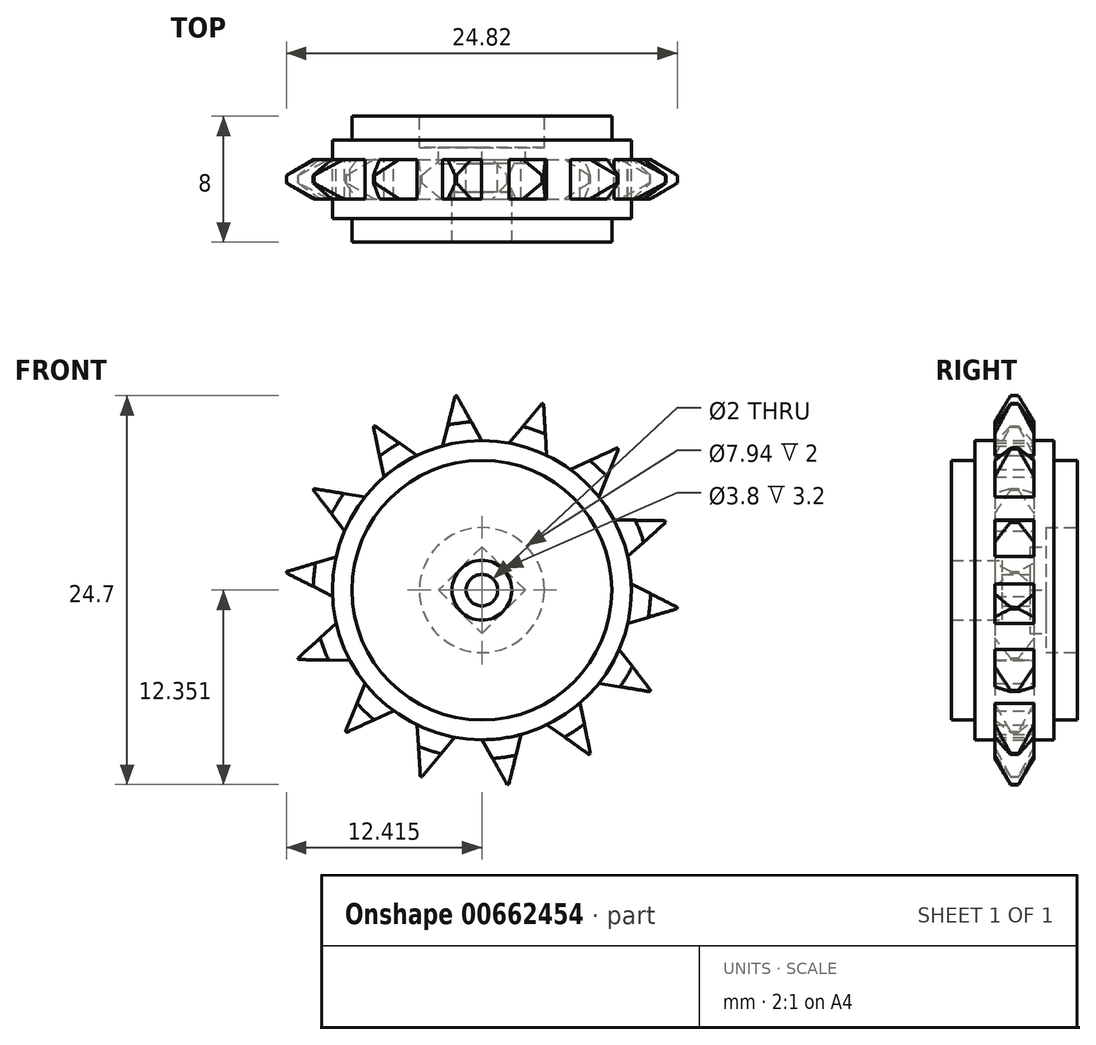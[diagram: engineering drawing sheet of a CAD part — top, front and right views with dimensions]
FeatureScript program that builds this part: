
annotation { "Feature Type Name" : "Feature", "Feature Type Description" : "" }
export const myFeature = defineFeature(function(context is Context, id is Id, definition is map)
    precondition{}
    {
        {
            var Q0;
            Q0=qCreatedBy(makeId("Front.planeOp"),FACE);
            var sketch = newSketch(context, id + "F0", { "sketchPlane" : qUnion([Q0])});
            skCircle(sketch, "E0.cCircle", {"center": v(-41.57, 57.03) * mm, "radius": 16.12 * mm, "construction": true});
            skLineSegment(sketch, "E0.0", {"start": v(-32.25, 43.87) * mm, "end": v(-37.32, 41.48) * mm});
            skLineSegment(sketch, "E0.1", {"start": v(-37.32, 41.48) * mm, "end": v(-42.9, 40.96) * mm});
            skLineSegment(sketch, "E0.2", {"start": v(-42.9, 40.96) * mm, "end": v(-48.3, 42.38) * mm});
            skLineSegment(sketch, "E0.3", {"start": v(-48.3, 42.38) * mm, "end": v(-52.91, 45.57) * mm});
            skLineSegment(sketch, "E0.4", {"start": v(-52.91, 45.57) * mm, "end": v(-56.15, 50.14) * mm});
            skLineSegment(sketch, "E0.5", {"start": v(-56.15, 50.14) * mm, "end": v(-57.63, 55.54) * mm});
            skLineSegment(sketch, "E0.6", {"start": v(-57.63, 55.54) * mm, "end": v(-57.17, 61.12) * mm});
            skLineSegment(sketch, "E0.7", {"start": v(-57.17, 61.12) * mm, "end": v(-54.83, 66.2) * mm});
            skLineSegment(sketch, "E0.8", {"start": v(-54.83, 66.2) * mm, "end": v(-50.9, 70.19) * mm});
            skLineSegment(sketch, "E0.9", {"start": v(-50.9, 70.19) * mm, "end": v(-45.83, 72.58) * mm});
            skLineSegment(sketch, "E0.10", {"start": v(-45.83, 72.58) * mm, "end": v(-40.25, 73.1) * mm});
            skLineSegment(sketch, "E0.11", {"start": v(-40.25, 73.1) * mm, "end": v(-34.84, 71.68) * mm});
            skLineSegment(sketch, "E0.12", {"start": v(-34.84, 71.68) * mm, "end": v(-30.23, 68.5) * mm});
            skLineSegment(sketch, "E0.13", {"start": v(-30.23, 68.5) * mm, "end": v(-27, 63.92) * mm});
            skLineSegment(sketch, "E0.14", {"start": v(-27, 63.92) * mm, "end": v(-25.52, 58.52) * mm});
            skLineSegment(sketch, "E0.15", {"start": v(-25.52, 58.52) * mm, "end": v(-25.98, 52.94) * mm});
            skLineSegment(sketch, "E0.16", {"start": v(-25.98, 52.94) * mm, "end": v(-28.31, 47.85) * mm});
            skLineSegment(sketch, "E0.17", {"start": v(-28.31, 47.85) * mm, "end": v(-32.25, 43.87) * mm});
            skCircle(sketch, "E1.cCircle", {"center": v(18.75, 75.94) * mm, "radius": 12.58 * mm, "construction": true});
            skLineSegment(sketch, "E1.0", {"start": v(29.55, 69.47) * mm, "end": v(25.67, 65.43) * mm});
            skLineSegment(sketch, "E1.1", {"start": v(25.67, 65.43) * mm, "end": v(20.43, 63.47) * mm});
            skLineSegment(sketch, "E1.2", {"start": v(20.43, 63.47) * mm, "end": v(14.85, 63.98) * mm});
            skLineSegment(sketch, "E1.3", {"start": v(14.85, 63.98) * mm, "end": v(10.05, 66.86) * mm});
            skLineSegment(sketch, "E1.4", {"start": v(10.05, 66.86) * mm, "end": v(6.97, 71.54) * mm});
            skLineSegment(sketch, "E1.5", {"start": v(6.97, 71.54) * mm, "end": v(6.22, 77.09) * mm});
            skLineSegment(sketch, "E1.6", {"start": v(6.22, 77.09) * mm, "end": v(7.96, 82.4) * mm});
            skLineSegment(sketch, "E1.7", {"start": v(7.96, 82.4) * mm, "end": v(11.84, 86.45) * mm});
            skLineSegment(sketch, "E1.8", {"start": v(11.84, 86.45) * mm, "end": v(17.08, 88.41) * mm});
            skLineSegment(sketch, "E1.9", {"start": v(17.08, 88.41) * mm, "end": v(22.66, 87.9) * mm});
            skLineSegment(sketch, "E1.10", {"start": v(22.66, 87.9) * mm, "end": v(27.46, 85.02) * mm});
            skLineSegment(sketch, "E1.11", {"start": v(27.46, 85.02) * mm, "end": v(30.54, 80.35) * mm});
            skLineSegment(sketch, "E1.12", {"start": v(30.54, 80.35) * mm, "end": v(31.29, 74.8) * mm});
            skLineSegment(sketch, "E1.13", {"start": v(31.29, 74.8) * mm, "end": v(29.55, 69.47) * mm});
            skLineSegment(sketch, "E2", {"start": v(7.96, 82.4) * mm, "end": v(18.75, 75.94) * mm});
            skLineSegment(sketch, "E3", {"start": v(18.75, 75.94) * mm, "end": v(17.08, 88.41) * mm});
            skLineSegment(sketch, "E4", {"start": v(13.36, 79.18) * mm, "end": v(11.84, 86.45) * mm});
            skLineSegment(sketch, "E5", {"start": v(17.92, 82.18) * mm, "end": v(11.84, 86.45) * mm});
            skLineSegment(sketch, "E6.1.0", {"start": v(15.3, 81.2) * mm, "end": v(7.96, 82.4) * mm});
            skLineSegment(sketch, "E6.1.1", {"start": v(12.49, 76.51) * mm, "end": v(7.96, 82.4) * mm});
            skLineSegment(sketch, "E6.2.0", {"start": v(13.36, 79.18) * mm, "end": v(6.22, 77.09) * mm});
            skLineSegment(sketch, "E6.2.1", {"start": v(12.86, 73.74) * mm, "end": v(6.22, 77.09) * mm});
            skLineSegment(sketch, "E6.3.0", {"start": v(12.49, 76.51) * mm, "end": v(6.97, 71.54) * mm});
            skLineSegment(sketch, "E6.3.1", {"start": v(14.4, 71.4) * mm, "end": v(6.97, 71.54) * mm});
            skLineSegment(sketch, "E6.4.0", {"start": v(12.86, 73.74) * mm, "end": v(10.05, 66.86) * mm});
            skLineSegment(sketch, "E6.4.1", {"start": v(16.8, 69.96) * mm, "end": v(10.05, 66.86) * mm});
            skLineSegment(sketch, "E6.5.0", {"start": v(14.4, 71.4) * mm, "end": v(14.85, 63.98) * mm});
            skLineSegment(sketch, "E6.5.1", {"start": v(19.6, 69.7) * mm, "end": v(14.85, 63.98) * mm});
            skLineSegment(sketch, "E6.6.0", {"start": v(16.8, 69.96) * mm, "end": v(20.43, 63.47) * mm});
            skLineSegment(sketch, "E6.6.1", {"start": v(22.21, 70.69) * mm, "end": v(20.43, 63.47) * mm});
            skLineSegment(sketch, "E6.7.0", {"start": v(19.6, 69.7) * mm, "end": v(25.67, 65.43) * mm});
            skLineSegment(sketch, "E6.7.1", {"start": v(24.15, 72.7) * mm, "end": v(25.67, 65.43) * mm});
            skLineSegment(sketch, "E6.8.0", {"start": v(22.21, 70.69) * mm, "end": v(29.55, 69.47) * mm});
            skLineSegment(sketch, "E6.8.1", {"start": v(25.02, 75.37) * mm, "end": v(29.55, 69.47) * mm});
            skLineSegment(sketch, "E6.9.0", {"start": v(24.15, 72.7) * mm, "end": v(31.29, 74.8) * mm});
            skLineSegment(sketch, "E6.9.1", {"start": v(24.65, 78.14) * mm, "end": v(31.29, 74.8) * mm});
            skLineSegment(sketch, "E6.10.0", {"start": v(25.02, 75.37) * mm, "end": v(30.54, 80.35) * mm});
            skLineSegment(sketch, "E6.10.1", {"start": v(23.1, 80.48) * mm, "end": v(30.54, 80.35) * mm});
            skLineSegment(sketch, "E6.11.0", {"start": v(24.65, 78.14) * mm, "end": v(27.46, 85.02) * mm});
            skLineSegment(sketch, "E6.11.1", {"start": v(20.7, 81.92) * mm, "end": v(27.46, 85.02) * mm});
            skLineSegment(sketch, "E6.12.0", {"start": v(23.1, 80.48) * mm, "end": v(22.66, 87.9) * mm});
            skLineSegment(sketch, "E6.12.1", {"start": v(17.92, 82.18) * mm, "end": v(22.66, 87.9) * mm});
            skLineSegment(sketch, "E6.13.0", {"start": v(20.7, 81.92) * mm, "end": v(17.08, 88.41) * mm});
            skLineSegment(sketch, "E6.13.1", {"start": v(15.3, 81.2) * mm, "end": v(17.08, 88.41) * mm});
            skCircle(sketch, "E7", {"center": v(18.75, 75.94) * mm, "radius": 12.46 * mm});
            skCircle(sketch, "E8", {"center": v(18.75, 75.94) * mm, "radius": 9.5 * mm});
            skCircle(sketch, "E9", {"center": v(18.75, 75.94) * mm, "radius": 8.25 * mm});
            skCircle(sketch, "E10.cCircle", {"center": v(18.75, 75.94) * mm, "radius": 2.65 * mm, "construction": true});
            skLineSegment(sketch, "E10.0", {"start": v(16.1, 75.94) * mm, "end": v(18.75, 78.6) * mm});
            skLineSegment(sketch, "E10.1", {"start": v(18.75, 78.6) * mm, "end": v(21.4, 75.94) * mm});
            skLineSegment(sketch, "E10.2", {"start": v(21.4, 75.94) * mm, "end": v(18.75, 73.29) * mm});
            skLineSegment(sketch, "E10.3", {"start": v(18.75, 73.29) * mm, "end": v(16.1, 75.94) * mm});
            skCircle(sketch, "E11", {"center": v(18.75, 75.94) * mm, "radius": 0.86 * mm});
            skSolve(sketch);
        }
        {
            var Q0;
            {var subQ27=sQuery(id+"F0.wireOp",EDGE,"E6.3.0");var subQ28=sQuery(id+"F0.wireOp",EDGE,"E6.1.1");var subQ29=makeQuery(id+"F0.imprint","INTERSECT",VERTEX,{"derivedFrom":[subQ28,subQ27]});Q0=makeQuery(id+"F0.imprint","IMPRINT",FACE,{"disambiguationData":[TD([[makeQuery(id+"F0.imprint","IMPRINT",EDGE,{"disambiguationData":[TD([[subQ29,-1.0]])],"derivedFrom":subQ28}),-1.0]])]});}
            var Q1;
            {var subQ3=sQuery(id+"F0.wireOp",EDGE,"E6.13.1");var subQ9=sQuery(id+"F0.wireOp",EDGE,"E6.1.0");var subQ11=makeQuery(id+"F0.imprint","INTERSECT",VERTEX,{"derivedFrom":[subQ9,subQ3]});Q1=makeQuery(id+"F0.imprint","IMPRINT",FACE,{"disambiguationData":[TD([[makeQuery(id+"F0.imprint","IMPRINT",EDGE,{"disambiguationData":[TD([[subQ11,-1.0]])],"derivedFrom":subQ9}),1.0]])]});}
            var Q2;
            {var subQ1=sQuery(id+"F0.wireOp",EDGE,"E6.1.0");var subQ5=sQuery(id+"F0.wireOp",EDGE,"E4");var subQ6=makeQuery(id+"F0.imprint","INTERSECT",VERTEX,{"derivedFrom":[subQ5,subQ1]});Q2=makeQuery(id+"F0.imprint","IMPRINT",FACE,{"disambiguationData":[TD([[makeQuery(id+"F0.imprint","IMPRINT",EDGE,{"disambiguationData":[TD([[subQ6,-1.0]])],"derivedFrom":subQ5}),-1.0]])]});}
            var Q3;
            {var subQ0=sQuery(id+"F0.wireOp",EDGE,"E6.2.0");var subQ5=sQuery(id+"F0.wireOp",EDGE,"E6.1.1");var subQ6=makeQuery(id+"F0.imprint","INTERSECT",VERTEX,{"derivedFrom":[subQ5,subQ0]});Q3=makeQuery(id+"F0.imprint","IMPRINT",FACE,{"disambiguationData":[TD([[makeQuery(id+"F0.imprint","IMPRINT",EDGE,{"disambiguationData":[TD([[subQ6,-1.0]])],"derivedFrom":subQ5}),-1.0]])]});}
            var Q4;
            {var subQ0=sQuery(id+"F0.wireOp",EDGE,"E6.3.0");var subQ1=sQuery(id+"F0.wireOp",EDGE,"E6.1.1");var subQ2=makeQuery(id+"F0.imprint","INTERSECT",VERTEX,{"derivedFrom":[subQ1,subQ0]});Q4=makeQuery(id+"F0.imprint","IMPRINT",FACE,{"disambiguationData":[TD([[makeQuery(id+"F0.imprint","IMPRINT",EDGE,{"disambiguationData":[TD([[subQ2,-1.0]])],"derivedFrom":subQ1}),1.0]])]});}
            var Q5;
            {var subQ0=sQuery(id+"F0.wireOp",EDGE,"E6.3.0");var subQ1=sQuery(id+"F0.wireOp",EDGE,"E6.2.1");var subQ2=makeQuery(id+"F0.imprint","INTERSECT",VERTEX,{"derivedFrom":[subQ1,subQ0]});Q5=makeQuery(id+"F0.imprint","IMPRINT",FACE,{"disambiguationData":[TD([[makeQuery(id+"F0.imprint","IMPRINT",EDGE,{"disambiguationData":[TD([[subQ2,-1.0]])],"derivedFrom":subQ1}),1.0]])]});}
            var Q6;
            {var subQ0=sQuery(id+"F0.wireOp",EDGE,"E6.2.0");var subQ1=sQuery(id+"F0.wireOp",EDGE,"E6.1.1");var subQ2=makeQuery(id+"F0.imprint","INTERSECT",VERTEX,{"derivedFrom":[subQ1,subQ0]});Q6=makeQuery(id+"F0.imprint","IMPRINT",FACE,{"disambiguationData":[TD([[makeQuery(id+"F0.imprint","IMPRINT",EDGE,{"disambiguationData":[TD([[subQ2,-1.0]])],"derivedFrom":subQ1}),1.0]])]});}
            var Q7;
            {var subQ0=sQuery(id+"F0.wireOp",EDGE,"E4");var subQ5=sQuery(id+"F0.wireOp",EDGE,"E6.1.0");var subQ6=makeQuery(id+"F0.imprint","INTERSECT",VERTEX,{"derivedFrom":[subQ0,subQ5]});Q7=makeQuery(id+"F0.imprint","IMPRINT",FACE,{"disambiguationData":[TD([[makeQuery(id+"F0.imprint","IMPRINT",EDGE,{"disambiguationData":[TD([[subQ6,-1.0]])],"derivedFrom":subQ5}),1.0]])]});}
            var Q8;
            {var subQ0=sQuery(id+"F0.wireOp",EDGE,"E6.1.0");var subQ1=sQuery(id+"F0.wireOp",EDGE,"E4");var subQ2=makeQuery(id+"F0.imprint","INTERSECT",VERTEX,{"derivedFrom":[subQ1,subQ0]});Q8=makeQuery(id+"F0.imprint","IMPRINT",FACE,{"disambiguationData":[TD([[makeQuery(id+"F0.imprint","IMPRINT",EDGE,{"disambiguationData":[TD([[subQ2,-1.0]])],"derivedFrom":subQ1}),1.0]])]});}
            var Q9;
            {var subQ0=sQuery(id+"F0.wireOp",EDGE,"E6.13.1");var subQ1=sQuery(id+"F0.wireOp",EDGE,"E5");var subQ2=makeQuery(id+"F0.imprint","INTERSECT",VERTEX,{"derivedFrom":[subQ1,subQ0]});Q9=makeQuery(id+"F0.imprint","IMPRINT",FACE,{"disambiguationData":[TD([[makeQuery(id+"F0.imprint","IMPRINT",EDGE,{"disambiguationData":[TD([[subQ2,-1.0]])],"derivedFrom":subQ1}),-1.0]])]});}
            var Q10;
            {var subQ0=sQuery(id+"F0.wireOp",EDGE,"E5");var subQ5=sQuery(id+"F0.wireOp",EDGE,"E6.13.1");var subQ7=makeQuery(id+"F0.imprint","INTERSECT",VERTEX,{"derivedFrom":[subQ0,subQ5]});Q10=makeQuery(id+"F0.imprint","IMPRINT",FACE,{"disambiguationData":[TD([[makeQuery(id+"F0.imprint","IMPRINT",EDGE,{"disambiguationData":[TD([[subQ7,-1.0]])],"derivedFrom":subQ5}),-1.0]])]});}
            var Q11;
            {var subQ0=sQuery(id+"F0.wireOp",EDGE,"E6.12.1");var subQ5=sQuery(id+"F0.wireOp",EDGE,"E6.13.0");var subQ6=makeQuery(id+"F0.imprint","INTERSECT",VERTEX,{"derivedFrom":[subQ0,subQ5]});Q11=makeQuery(id+"F0.imprint","IMPRINT",FACE,{"disambiguationData":[TD([[makeQuery(id+"F0.imprint","IMPRINT",EDGE,{"disambiguationData":[TD([[subQ6,-1.0]])],"derivedFrom":subQ5}),1.0]])]});}
            var Q12;
            {var subQ0=sQuery(id+"F0.wireOp",EDGE,"E6.13.0");var subQ1=sQuery(id+"F0.wireOp",EDGE,"E6.12.1");var subQ2=makeQuery(id+"F0.imprint","INTERSECT",VERTEX,{"derivedFrom":[subQ1,subQ0]});Q12=makeQuery(id+"F0.imprint","IMPRINT",FACE,{"disambiguationData":[TD([[makeQuery(id+"F0.imprint","IMPRINT",EDGE,{"disambiguationData":[TD([[subQ2,-1.0]])],"derivedFrom":subQ1}),1.0]])]});}
            var Q13;
            {var subQ0=sQuery(id+"F0.wireOp",EDGE,"E6.13.0");var subQ1=sQuery(id+"F0.wireOp",EDGE,"E6.11.1");var subQ2=makeQuery(id+"F0.imprint","INTERSECT",VERTEX,{"derivedFrom":[subQ1,subQ0]});Q13=makeQuery(id+"F0.imprint","IMPRINT",FACE,{"disambiguationData":[TD([[makeQuery(id+"F0.imprint","IMPRINT",EDGE,{"disambiguationData":[TD([[subQ2,-1.0]])],"derivedFrom":subQ1}),1.0]])]});}
            var Q14;
            {var subQ0=sQuery(id+"F0.wireOp",EDGE,"E6.12.0");var subQ1=sQuery(id+"F0.wireOp",EDGE,"E6.11.1");var subQ2=makeQuery(id+"F0.imprint","INTERSECT",VERTEX,{"derivedFrom":[subQ1,subQ0]});Q14=makeQuery(id+"F0.imprint","IMPRINT",FACE,{"disambiguationData":[TD([[makeQuery(id+"F0.imprint","IMPRINT",EDGE,{"disambiguationData":[TD([[subQ2,-1.0]])],"derivedFrom":subQ1}),1.0]])]});}
            var Q15;
            {var subQ0=sQuery(id+"F0.wireOp",EDGE,"E6.12.0");var subQ1=sQuery(id+"F0.wireOp",EDGE,"E6.10.1");var subQ2=makeQuery(id+"F0.imprint","INTERSECT",VERTEX,{"derivedFrom":[subQ1,subQ0]});Q15=makeQuery(id+"F0.imprint","IMPRINT",FACE,{"disambiguationData":[TD([[makeQuery(id+"F0.imprint","IMPRINT",EDGE,{"disambiguationData":[TD([[subQ2,-1.0]])],"derivedFrom":subQ1}),1.0]])]});}
            var Q16;
            {var subQ0=sQuery(id+"F0.wireOp",EDGE,"E6.11.0");var subQ1=sQuery(id+"F0.wireOp",EDGE,"E6.10.1");var subQ2=makeQuery(id+"F0.imprint","INTERSECT",VERTEX,{"derivedFrom":[subQ1,subQ0]});Q16=makeQuery(id+"F0.imprint","IMPRINT",FACE,{"disambiguationData":[TD([[makeQuery(id+"F0.imprint","IMPRINT",EDGE,{"disambiguationData":[TD([[subQ2,-1.0]])],"derivedFrom":subQ1}),1.0]])]});}
            var Q17;
            {var subQ0=sQuery(id+"F0.wireOp",EDGE,"E6.11.0");var subQ1=sQuery(id+"F0.wireOp",EDGE,"E6.9.1");var subQ2=makeQuery(id+"F0.imprint","INTERSECT",VERTEX,{"derivedFrom":[subQ1,subQ0]});Q17=makeQuery(id+"F0.imprint","IMPRINT",FACE,{"disambiguationData":[TD([[makeQuery(id+"F0.imprint","IMPRINT",EDGE,{"disambiguationData":[TD([[subQ2,-1.0]])],"derivedFrom":subQ1}),1.0]])]});}
            var Q18;
            {var subQ0=sQuery(id+"F0.wireOp",EDGE,"E6.10.0");var subQ1=sQuery(id+"F0.wireOp",EDGE,"E6.9.1");var subQ2=makeQuery(id+"F0.imprint","INTERSECT",VERTEX,{"derivedFrom":[subQ1,subQ0]});Q18=makeQuery(id+"F0.imprint","IMPRINT",FACE,{"disambiguationData":[TD([[makeQuery(id+"F0.imprint","IMPRINT",EDGE,{"disambiguationData":[TD([[subQ2,-1.0]])],"derivedFrom":subQ1}),1.0]])]});}
            var Q19;
            {var subQ0=sQuery(id+"F0.wireOp",EDGE,"E6.10.0");var subQ1=sQuery(id+"F0.wireOp",EDGE,"E6.8.1");var subQ2=makeQuery(id+"F0.imprint","INTERSECT",VERTEX,{"derivedFrom":[subQ1,subQ0]});Q19=makeQuery(id+"F0.imprint","IMPRINT",FACE,{"disambiguationData":[TD([[makeQuery(id+"F0.imprint","IMPRINT",EDGE,{"disambiguationData":[TD([[subQ2,-1.0]])],"derivedFrom":subQ1}),1.0]])]});}
            var Q20;
            {var subQ0=sQuery(id+"F0.wireOp",EDGE,"E6.9.0");var subQ1=sQuery(id+"F0.wireOp",EDGE,"E6.8.1");var subQ2=makeQuery(id+"F0.imprint","INTERSECT",VERTEX,{"derivedFrom":[subQ1,subQ0]});Q20=makeQuery(id+"F0.imprint","IMPRINT",FACE,{"disambiguationData":[TD([[makeQuery(id+"F0.imprint","IMPRINT",EDGE,{"disambiguationData":[TD([[subQ2,-1.0]])],"derivedFrom":subQ1}),1.0]])]});}
            var Q21;
            {var subQ0=sQuery(id+"F0.wireOp",EDGE,"E6.9.0");var subQ1=sQuery(id+"F0.wireOp",EDGE,"E6.7.1");var subQ2=makeQuery(id+"F0.imprint","INTERSECT",VERTEX,{"derivedFrom":[subQ1,subQ0]});Q21=makeQuery(id+"F0.imprint","IMPRINT",FACE,{"disambiguationData":[TD([[makeQuery(id+"F0.imprint","IMPRINT",EDGE,{"disambiguationData":[TD([[subQ2,-1.0]])],"derivedFrom":subQ1}),1.0]])]});}
            var Q22;
            {var subQ0=sQuery(id+"F0.wireOp",EDGE,"E6.8.0");var subQ1=sQuery(id+"F0.wireOp",EDGE,"E6.6.1");var subQ2=makeQuery(id+"F0.imprint","INTERSECT",VERTEX,{"derivedFrom":[subQ1,subQ0]});Q22=makeQuery(id+"F0.imprint","IMPRINT",FACE,{"disambiguationData":[TD([[makeQuery(id+"F0.imprint","IMPRINT",EDGE,{"disambiguationData":[TD([[subQ2,-1.0]])],"derivedFrom":subQ1}),1.0]])]});}
            var Q23;
            {var subQ0=sQuery(id+"F0.wireOp",EDGE,"E6.7.0");var subQ1=sQuery(id+"F0.wireOp",EDGE,"E6.6.1");var subQ2=makeQuery(id+"F0.imprint","INTERSECT",VERTEX,{"derivedFrom":[subQ1,subQ0]});Q23=makeQuery(id+"F0.imprint","IMPRINT",FACE,{"disambiguationData":[TD([[makeQuery(id+"F0.imprint","IMPRINT",EDGE,{"disambiguationData":[TD([[subQ2,-1.0]])],"derivedFrom":subQ1}),1.0]])]});}
            var Q24;
            {var subQ0=sQuery(id+"F0.wireOp",EDGE,"E6.7.0");var subQ1=sQuery(id+"F0.wireOp",EDGE,"E6.5.1");var subQ2=makeQuery(id+"F0.imprint","INTERSECT",VERTEX,{"derivedFrom":[subQ1,subQ0]});Q24=makeQuery(id+"F0.imprint","IMPRINT",FACE,{"disambiguationData":[TD([[makeQuery(id+"F0.imprint","IMPRINT",EDGE,{"disambiguationData":[TD([[subQ2,-1.0]])],"derivedFrom":subQ1}),1.0]])]});}
            var Q25;
            {var subQ0=sQuery(id+"F0.wireOp",EDGE,"E6.6.0");var subQ1=sQuery(id+"F0.wireOp",EDGE,"E6.5.1");var subQ2=makeQuery(id+"F0.imprint","INTERSECT",VERTEX,{"derivedFrom":[subQ1,subQ0]});Q25=makeQuery(id+"F0.imprint","IMPRINT",FACE,{"disambiguationData":[TD([[makeQuery(id+"F0.imprint","IMPRINT",EDGE,{"disambiguationData":[TD([[subQ2,-1.0]])],"derivedFrom":subQ1}),1.0]])]});}
            var Q26;
            {var subQ0=sQuery(id+"F0.wireOp",EDGE,"E6.4.0");var subQ1=sQuery(id+"F0.wireOp",EDGE,"E6.3.1");var subQ2=makeQuery(id+"F0.imprint","INTERSECT",VERTEX,{"derivedFrom":[subQ1,subQ0]});Q26=makeQuery(id+"F0.imprint","IMPRINT",FACE,{"disambiguationData":[TD([[makeQuery(id+"F0.imprint","IMPRINT",EDGE,{"disambiguationData":[TD([[subQ2,-1.0]])],"derivedFrom":subQ1}),1.0]])]});}
            var Q27;
            {var subQ0=sQuery(id+"F0.wireOp",EDGE,"E6.4.0");var subQ1=sQuery(id+"F0.wireOp",EDGE,"E6.2.1");var subQ2=makeQuery(id+"F0.imprint","INTERSECT",VERTEX,{"derivedFrom":[subQ1,subQ0]});Q27=makeQuery(id+"F0.imprint","IMPRINT",FACE,{"disambiguationData":[TD([[makeQuery(id+"F0.imprint","IMPRINT",EDGE,{"disambiguationData":[TD([[subQ2,-1.0]])],"derivedFrom":subQ1}),1.0]])]});}
            var Q28;
            {var subQ0=sQuery(id+"F0.wireOp",EDGE,"E6.5.0");var subQ1=sQuery(id+"F0.wireOp",EDGE,"E6.3.1");var subQ2=makeQuery(id+"F0.imprint","INTERSECT",VERTEX,{"derivedFrom":[subQ1,subQ0]});Q28=makeQuery(id+"F0.imprint","IMPRINT",FACE,{"disambiguationData":[TD([[makeQuery(id+"F0.imprint","IMPRINT",EDGE,{"disambiguationData":[TD([[subQ2,-1.0]])],"derivedFrom":subQ1}),1.0]])]});}
            var Q29;
            {var subQ0=sQuery(id+"F0.wireOp",EDGE,"E6.5.0");var subQ1=sQuery(id+"F0.wireOp",EDGE,"E6.4.1");var subQ2=makeQuery(id+"F0.imprint","INTERSECT",VERTEX,{"derivedFrom":[subQ1,subQ0]});Q29=makeQuery(id+"F0.imprint","IMPRINT",FACE,{"disambiguationData":[TD([[makeQuery(id+"F0.imprint","IMPRINT",EDGE,{"disambiguationData":[TD([[subQ2,-1.0]])],"derivedFrom":subQ1}),1.0]])]});}
            var Q30;
            {var subQ0=sQuery(id+"F0.wireOp",EDGE,"E6.6.0");var subQ1=sQuery(id+"F0.wireOp",EDGE,"E6.4.1");var subQ2=makeQuery(id+"F0.imprint","INTERSECT",VERTEX,{"derivedFrom":[subQ1,subQ0]});Q30=makeQuery(id+"F0.imprint","IMPRINT",FACE,{"disambiguationData":[TD([[makeQuery(id+"F0.imprint","IMPRINT",EDGE,{"disambiguationData":[TD([[subQ2,-1.0]])],"derivedFrom":subQ1}),1.0]])]});}
            var Q31;
            {var subQ0=sQuery(id+"F0.wireOp",EDGE,"E6.8.0");var subQ1=sQuery(id+"F0.wireOp",EDGE,"E6.7.1");var subQ2=makeQuery(id+"F0.imprint","INTERSECT",VERTEX,{"derivedFrom":[subQ1,subQ0]});Q31=makeQuery(id+"F0.imprint","IMPRINT",FACE,{"disambiguationData":[TD([[makeQuery(id+"F0.imprint","IMPRINT",EDGE,{"disambiguationData":[TD([[subQ2,-1.0]])],"derivedFrom":subQ1}),1.0]])]});}
            var Q32;
            {var subQ0=sQuery(id+"F0.wireOp",EDGE,"E10.1");Q32=makeQuery(id+"F0.imprint","IMPRINT",FACE,{"disambiguationData":[TD([[makeQuery(id+"F0.imprint","IMPRINT",EDGE,{"derivedFrom":subQ0}),-1.0]])]});}
            var Q33;
            {var subQ0=sQuery(id+"F0.wireOp",EDGE,"E3");var subQ1=sQuery(id+"F0.wireOp",EDGE,"E2");var subQ2=makeQuery(id+"F0.imprint","INTERSECT",VERTEX,{"derivedFrom":[subQ1,subQ0]});Q33=makeQuery(id+"F0.imprint","IMPRINT",FACE,{"disambiguationData":[TD([[makeQuery(id+"F0.imprint","IMPRINT",EDGE,{"disambiguationData":[TD([[subQ2,1.0]])],"derivedFrom":subQ1}),-1.0]])]});}
            var Q34;
            {var subQ0=sQuery(id+"F0.wireOp",EDGE,"E10.0");var subQ1=sQuery(id+"F0.wireOp",EDGE,"E2");var subQ2=makeQuery(id+"F0.imprint","INTERSECT",VERTEX,{"derivedFrom":[subQ1,subQ0]});Q34=makeQuery(id+"F0.imprint","IMPRINT",FACE,{"disambiguationData":[TD([[makeQuery(id+"F0.imprint","IMPRINT",EDGE,{"disambiguationData":[TD([[subQ2,-1.0]])],"derivedFrom":subQ1}),1.0]])]});}
            var Q35;
            {var subQ0=sQuery(id+"F0.wireOp",EDGE,"E3");var subQ1=sQuery(id+"F0.wireOp",EDGE,"E2");var subQ2=makeQuery(id+"F0.imprint","INTERSECT",VERTEX,{"derivedFrom":[subQ1,subQ0]});Q35=makeQuery(id+"F0.imprint","IMPRINT",FACE,{"disambiguationData":[TD([[makeQuery(id+"F0.imprint","IMPRINT",EDGE,{"disambiguationData":[TD([[subQ2,1.0]])],"derivedFrom":subQ1}),1.0]])]});}
            extrude(context, id + "F1", {"entities" : qUnion([Q0, Q1, Q2, Q3, Q4, Q5, Q6, Q7, Q8, Q9, Q10, Q11, Q12, Q13, Q14, Q15, Q16, Q17, Q18, Q19, Q20, Q21, Q22, Q23, Q24, Q25, Q26, Q27, Q28, Q29, Q30, Q31, Q32, Q33, Q34, Q35]), "endBound" : BoundingType.SYMMETRIC, "oppositeDirection" : true, "depth" : 8 * mm, "offsetDistance" : 25 * mm});
        }
        {
            var Q0;
            {var subQ0=sQuery(id+"F0.wireOp",EDGE,"E9");var subQ1=sQuery(id+"F0.wireOp",EDGE,"E6.5.0");var subQ2=makeQuery(id+"F0.imprint","INTERSECT",VERTEX,{"derivedFrom":[subQ1,subQ0]});Q0=makeQuery(id+"F0.imprint","IMPRINT",FACE,{"disambiguationData":[TD([[makeQuery(id+"F0.imprint","IMPRINT",EDGE,{"disambiguationData":[TD([[subQ2,-1.0]])],"derivedFrom":subQ1}),1.0]])]});}
            var Q1;
            {var subQ0=sQuery(id+"F0.wireOp",EDGE,"E9");var subQ1=sQuery(id+"F0.wireOp",EDGE,"E6.6.0");var subQ2=makeQuery(id+"F0.imprint","INTERSECT",VERTEX,{"derivedFrom":[subQ1,subQ0]});Q1=makeQuery(id+"F0.imprint","IMPRINT",FACE,{"disambiguationData":[TD([[makeQuery(id+"F0.imprint","IMPRINT",EDGE,{"disambiguationData":[TD([[subQ2,-1.0]])],"derivedFrom":subQ1}),1.0]])]});}
            var Q2;
            {var subQ0=sQuery(id+"F0.wireOp",EDGE,"E9");var subQ1=sQuery(id+"F0.wireOp",EDGE,"E6.6.1");var subQ2=makeQuery(id+"F0.imprint","INTERSECT",VERTEX,{"derivedFrom":[subQ1,subQ0]});Q2=makeQuery(id+"F0.imprint","IMPRINT",FACE,{"disambiguationData":[TD([[makeQuery(id+"F0.imprint","IMPRINT",EDGE,{"disambiguationData":[TD([[subQ2,-1.0]])],"derivedFrom":subQ1}),1.0]])]});}
            var Q3;
            {var subQ0=sQuery(id+"F0.wireOp",EDGE,"E9");var subQ1=sQuery(id+"F0.wireOp",EDGE,"E6.5.1");var subQ2=makeQuery(id+"F0.imprint","INTERSECT",VERTEX,{"derivedFrom":[subQ1,subQ0]});Q3=makeQuery(id+"F0.imprint","IMPRINT",FACE,{"disambiguationData":[TD([[makeQuery(id+"F0.imprint","IMPRINT",EDGE,{"disambiguationData":[TD([[subQ2,-1.0]])],"derivedFrom":subQ1}),1.0]])]});}
            var Q4;
            {var subQ0=sQuery(id+"F0.wireOp",EDGE,"E9");var subQ1=sQuery(id+"F0.wireOp",EDGE,"E6.7.0");var subQ2=makeQuery(id+"F0.imprint","INTERSECT",VERTEX,{"derivedFrom":[subQ1,subQ0]});Q4=makeQuery(id+"F0.imprint","IMPRINT",FACE,{"disambiguationData":[TD([[makeQuery(id+"F0.imprint","IMPRINT",EDGE,{"disambiguationData":[TD([[subQ2,-1.0]])],"derivedFrom":subQ1}),1.0]])]});}
            var Q5;
            {var subQ0=sQuery(id+"F0.wireOp",EDGE,"E9");var subQ1=sQuery(id+"F0.wireOp",EDGE,"E6.7.1");var subQ2=makeQuery(id+"F0.imprint","INTERSECT",VERTEX,{"derivedFrom":[subQ1,subQ0]});Q5=makeQuery(id+"F0.imprint","IMPRINT",FACE,{"disambiguationData":[TD([[makeQuery(id+"F0.imprint","IMPRINT",EDGE,{"disambiguationData":[TD([[subQ2,-1.0]])],"derivedFrom":subQ1}),1.0]])]});}
            var Q6;
            {var subQ0=sQuery(id+"F0.wireOp",EDGE,"E9");var subQ1=sQuery(id+"F0.wireOp",EDGE,"E6.8.0");var subQ2=makeQuery(id+"F0.imprint","INTERSECT",VERTEX,{"derivedFrom":[subQ1,subQ0]});Q6=makeQuery(id+"F0.imprint","IMPRINT",FACE,{"disambiguationData":[TD([[makeQuery(id+"F0.imprint","IMPRINT",EDGE,{"disambiguationData":[TD([[subQ2,-1.0]])],"derivedFrom":subQ1}),1.0]])]});}
            var Q7;
            {var subQ0=sQuery(id+"F0.wireOp",EDGE,"E9");var subQ1=sQuery(id+"F0.wireOp",EDGE,"E6.8.1");var subQ2=makeQuery(id+"F0.imprint","INTERSECT",VERTEX,{"derivedFrom":[subQ1,subQ0]});Q7=makeQuery(id+"F0.imprint","IMPRINT",FACE,{"disambiguationData":[TD([[makeQuery(id+"F0.imprint","IMPRINT",EDGE,{"disambiguationData":[TD([[subQ2,-1.0]])],"derivedFrom":subQ1}),1.0]])]});}
            var Q8;
            {var subQ0=sQuery(id+"F0.wireOp",EDGE,"E9");var subQ1=sQuery(id+"F0.wireOp",EDGE,"E6.9.0");var subQ2=makeQuery(id+"F0.imprint","INTERSECT",VERTEX,{"derivedFrom":[subQ1,subQ0]});Q8=makeQuery(id+"F0.imprint","IMPRINT",FACE,{"disambiguationData":[TD([[makeQuery(id+"F0.imprint","IMPRINT",EDGE,{"disambiguationData":[TD([[subQ2,-1.0]])],"derivedFrom":subQ1}),1.0]])]});}
            var Q9;
            {var subQ0=sQuery(id+"F0.wireOp",EDGE,"E9");var subQ1=sQuery(id+"F0.wireOp",EDGE,"E6.9.1");var subQ2=makeQuery(id+"F0.imprint","INTERSECT",VERTEX,{"derivedFrom":[subQ1,subQ0]});Q9=makeQuery(id+"F0.imprint","IMPRINT",FACE,{"disambiguationData":[TD([[makeQuery(id+"F0.imprint","IMPRINT",EDGE,{"disambiguationData":[TD([[subQ2,-1.0]])],"derivedFrom":subQ1}),1.0]])]});}
            var Q10;
            {var subQ0=sQuery(id+"F0.wireOp",EDGE,"E9");var subQ1=sQuery(id+"F0.wireOp",EDGE,"E6.10.0");var subQ2=makeQuery(id+"F0.imprint","INTERSECT",VERTEX,{"derivedFrom":[subQ1,subQ0]});Q10=makeQuery(id+"F0.imprint","IMPRINT",FACE,{"disambiguationData":[TD([[makeQuery(id+"F0.imprint","IMPRINT",EDGE,{"disambiguationData":[TD([[subQ2,-1.0]])],"derivedFrom":subQ1}),1.0]])]});}
            var Q11;
            {var subQ0=sQuery(id+"F0.wireOp",EDGE,"E9");var subQ1=sQuery(id+"F0.wireOp",EDGE,"E6.10.1");var subQ2=makeQuery(id+"F0.imprint","INTERSECT",VERTEX,{"derivedFrom":[subQ1,subQ0]});Q11=makeQuery(id+"F0.imprint","IMPRINT",FACE,{"disambiguationData":[TD([[makeQuery(id+"F0.imprint","IMPRINT",EDGE,{"disambiguationData":[TD([[subQ2,-1.0]])],"derivedFrom":subQ1}),1.0]])]});}
            var Q12;
            {var subQ0=sQuery(id+"F0.wireOp",EDGE,"E9");var subQ1=sQuery(id+"F0.wireOp",EDGE,"E6.11.0");var subQ2=makeQuery(id+"F0.imprint","INTERSECT",VERTEX,{"derivedFrom":[subQ1,subQ0]});Q12=makeQuery(id+"F0.imprint","IMPRINT",FACE,{"disambiguationData":[TD([[makeQuery(id+"F0.imprint","IMPRINT",EDGE,{"disambiguationData":[TD([[subQ2,-1.0]])],"derivedFrom":subQ1}),1.0]])]});}
            var Q13;
            {var subQ0=sQuery(id+"F0.wireOp",EDGE,"E9");var subQ1=sQuery(id+"F0.wireOp",EDGE,"E6.11.1");var subQ2=makeQuery(id+"F0.imprint","INTERSECT",VERTEX,{"derivedFrom":[subQ1,subQ0]});Q13=makeQuery(id+"F0.imprint","IMPRINT",FACE,{"disambiguationData":[TD([[makeQuery(id+"F0.imprint","IMPRINT",EDGE,{"disambiguationData":[TD([[subQ2,-1.0]])],"derivedFrom":subQ1}),1.0]])]});}
            var Q14;
            {var subQ0=sQuery(id+"F0.wireOp",EDGE,"E9");var subQ1=sQuery(id+"F0.wireOp",EDGE,"E6.12.1");var subQ2=makeQuery(id+"F0.imprint","INTERSECT",VERTEX,{"derivedFrom":[subQ1,subQ0]});Q14=makeQuery(id+"F0.imprint","IMPRINT",FACE,{"disambiguationData":[TD([[makeQuery(id+"F0.imprint","IMPRINT",EDGE,{"disambiguationData":[TD([[subQ2,-1.0]])],"derivedFrom":subQ1}),1.0]])]});}
            var Q15;
            {var subQ0=sQuery(id+"F0.wireOp",EDGE,"E9");var subQ1=sQuery(id+"F0.wireOp",EDGE,"E3");var subQ2=makeQuery(id+"F0.imprint","INTERSECT",VERTEX,{"derivedFrom":[subQ1,subQ0]});Q15=makeQuery(id+"F0.imprint","IMPRINT",FACE,{"disambiguationData":[TD([[makeQuery(id+"F0.imprint","IMPRINT",EDGE,{"disambiguationData":[TD([[subQ2,-1.0]])],"derivedFrom":subQ1}),-1.0]])]});}
            var Q16;
            {var subQ0=sQuery(id+"F0.wireOp",EDGE,"E9");var subQ1=sQuery(id+"F0.wireOp",EDGE,"E6.12.0");var subQ2=makeQuery(id+"F0.imprint","INTERSECT",VERTEX,{"derivedFrom":[subQ1,subQ0]});Q16=makeQuery(id+"F0.imprint","IMPRINT",FACE,{"disambiguationData":[TD([[makeQuery(id+"F0.imprint","IMPRINT",EDGE,{"disambiguationData":[TD([[subQ2,-1.0]])],"derivedFrom":subQ1}),1.0]])]});}
            var Q17;
            {var subQ0=sQuery(id+"F0.wireOp",EDGE,"E9");var subQ1=sQuery(id+"F0.wireOp",EDGE,"E3");var subQ2=makeQuery(id+"F0.imprint","INTERSECT",VERTEX,{"derivedFrom":[subQ1,subQ0]});Q17=makeQuery(id+"F0.imprint","IMPRINT",FACE,{"disambiguationData":[TD([[makeQuery(id+"F0.imprint","IMPRINT",EDGE,{"disambiguationData":[TD([[subQ2,-1.0]])],"derivedFrom":subQ1}),1.0]])]});}
            var Q18;
            {var subQ0=sQuery(id+"F0.wireOp",EDGE,"E9");var subQ1=sQuery(id+"F0.wireOp",EDGE,"E5");var subQ2=makeQuery(id+"F0.imprint","INTERSECT",VERTEX,{"derivedFrom":[subQ1,subQ0]});Q18=makeQuery(id+"F0.imprint","IMPRINT",FACE,{"disambiguationData":[TD([[makeQuery(id+"F0.imprint","IMPRINT",EDGE,{"disambiguationData":[TD([[subQ2,-1.0]])],"derivedFrom":subQ1}),-1.0]])]});}
            var Q19;
            {var subQ0=sQuery(id+"F0.wireOp",EDGE,"E9");var subQ1=sQuery(id+"F0.wireOp",EDGE,"E4");var subQ2=makeQuery(id+"F0.imprint","INTERSECT",VERTEX,{"derivedFrom":[subQ1,subQ0]});Q19=makeQuery(id+"F0.imprint","IMPRINT",FACE,{"disambiguationData":[TD([[makeQuery(id+"F0.imprint","IMPRINT",EDGE,{"disambiguationData":[TD([[subQ2,-1.0]])],"derivedFrom":subQ1}),-1.0]])]});}
            var Q20;
            {var subQ0=sQuery(id+"F0.wireOp",EDGE,"E9");var subQ1=sQuery(id+"F0.wireOp",EDGE,"E4");var subQ2=makeQuery(id+"F0.imprint","INTERSECT",VERTEX,{"derivedFrom":[subQ1,subQ0]});Q20=makeQuery(id+"F0.imprint","IMPRINT",FACE,{"disambiguationData":[TD([[makeQuery(id+"F0.imprint","IMPRINT",EDGE,{"disambiguationData":[TD([[subQ2,-1.0]])],"derivedFrom":subQ1}),1.0]])]});}
            var Q21;
            {var subQ0=sQuery(id+"F0.wireOp",EDGE,"E8");var subQ1=sQuery(id+"F0.wireOp",EDGE,"E2");var subQ2=makeQuery(id+"F0.imprint","INTERSECT",VERTEX,{"derivedFrom":[subQ1,subQ0]});Q21=makeQuery(id+"F0.imprint","IMPRINT",FACE,{"disambiguationData":[TD([[makeQuery(id+"F0.imprint","IMPRINT",EDGE,{"disambiguationData":[TD([[subQ2,-1.0]])],"derivedFrom":subQ1}),1.0]])]});}
            var Q22;
            {var subQ0=sQuery(id+"F0.wireOp",EDGE,"E8");var subQ1=sQuery(id+"F0.wireOp",EDGE,"E2");var subQ2=makeQuery(id+"F0.imprint","INTERSECT",VERTEX,{"derivedFrom":[subQ1,subQ0]});Q22=makeQuery(id+"F0.imprint","IMPRINT",FACE,{"disambiguationData":[TD([[makeQuery(id+"F0.imprint","IMPRINT",EDGE,{"disambiguationData":[TD([[subQ2,-1.0]])],"derivedFrom":subQ1}),-1.0]])]});}
            var Q23;
            {var subQ0=sQuery(id+"F0.wireOp",EDGE,"E9");var subQ1=sQuery(id+"F0.wireOp",EDGE,"E6.1.1");var subQ2=makeQuery(id+"F0.imprint","INTERSECT",VERTEX,{"derivedFrom":[subQ1,subQ0]});Q23=makeQuery(id+"F0.imprint","IMPRINT",FACE,{"disambiguationData":[TD([[makeQuery(id+"F0.imprint","IMPRINT",EDGE,{"disambiguationData":[TD([[subQ2,-1.0]])],"derivedFrom":subQ1}),1.0]])]});}
            var Q24;
            {var subQ0=sQuery(id+"F0.wireOp",EDGE,"E9");var subQ1=sQuery(id+"F0.wireOp",EDGE,"E6.2.0");var subQ2=makeQuery(id+"F0.imprint","INTERSECT",VERTEX,{"derivedFrom":[subQ1,subQ0]});Q24=makeQuery(id+"F0.imprint","IMPRINT",FACE,{"disambiguationData":[TD([[makeQuery(id+"F0.imprint","IMPRINT",EDGE,{"disambiguationData":[TD([[subQ2,-1.0]])],"derivedFrom":subQ1}),1.0]])]});}
            var Q25;
            {var subQ0=sQuery(id+"F0.wireOp",EDGE,"E9");var subQ1=sQuery(id+"F0.wireOp",EDGE,"E6.2.1");var subQ2=makeQuery(id+"F0.imprint","INTERSECT",VERTEX,{"derivedFrom":[subQ1,subQ0]});Q25=makeQuery(id+"F0.imprint","IMPRINT",FACE,{"disambiguationData":[TD([[makeQuery(id+"F0.imprint","IMPRINT",EDGE,{"disambiguationData":[TD([[subQ2,-1.0]])],"derivedFrom":subQ1}),1.0]])]});}
            var Q26;
            {var subQ0=sQuery(id+"F0.wireOp",EDGE,"E9");var subQ1=sQuery(id+"F0.wireOp",EDGE,"E6.3.0");var subQ2=makeQuery(id+"F0.imprint","INTERSECT",VERTEX,{"derivedFrom":[subQ1,subQ0]});Q26=makeQuery(id+"F0.imprint","IMPRINT",FACE,{"disambiguationData":[TD([[makeQuery(id+"F0.imprint","IMPRINT",EDGE,{"disambiguationData":[TD([[subQ2,-1.0]])],"derivedFrom":subQ1}),1.0]])]});}
            var Q27;
            {var subQ0=sQuery(id+"F0.wireOp",EDGE,"E9");var subQ1=sQuery(id+"F0.wireOp",EDGE,"E6.3.1");var subQ2=makeQuery(id+"F0.imprint","INTERSECT",VERTEX,{"derivedFrom":[subQ1,subQ0]});Q27=makeQuery(id+"F0.imprint","IMPRINT",FACE,{"disambiguationData":[TD([[makeQuery(id+"F0.imprint","IMPRINT",EDGE,{"disambiguationData":[TD([[subQ2,-1.0]])],"derivedFrom":subQ1}),1.0]])]});}
            var Q28;
            {var subQ0=sQuery(id+"F0.wireOp",EDGE,"E9");var subQ1=sQuery(id+"F0.wireOp",EDGE,"E6.4.0");var subQ2=makeQuery(id+"F0.imprint","INTERSECT",VERTEX,{"derivedFrom":[subQ1,subQ0]});Q28=makeQuery(id+"F0.imprint","IMPRINT",FACE,{"disambiguationData":[TD([[makeQuery(id+"F0.imprint","IMPRINT",EDGE,{"disambiguationData":[TD([[subQ2,-1.0]])],"derivedFrom":subQ1}),1.0]])]});}
            var Q29;
            {var subQ0=sQuery(id+"F0.wireOp",EDGE,"E9");var subQ1=sQuery(id+"F0.wireOp",EDGE,"E6.4.1");var subQ2=makeQuery(id+"F0.imprint","INTERSECT",VERTEX,{"derivedFrom":[subQ1,subQ0]});Q29=makeQuery(id+"F0.imprint","IMPRINT",FACE,{"disambiguationData":[TD([[makeQuery(id+"F0.imprint","IMPRINT",EDGE,{"disambiguationData":[TD([[subQ2,-1.0]])],"derivedFrom":subQ1}),1.0]])]});}
            extrude(context, id + "F2", {"entities" : qUnion([Q0, Q1, Q2, Q3, Q4, Q5, Q6, Q7, Q8, Q9, Q10, Q11, Q12, Q13, Q14, Q15, Q16, Q17, Q18, Q19, Q20, Q21, Q22, Q23, Q24, Q25, Q26, Q27, Q28, Q29]), "operationType" : NewBodyOperationType.ADD, "endBound" : BoundingType.SYMMETRIC, "depth" : 5 * mm, "offsetDistance" : 25 * mm});
        }
        {
            var Q0;
            {var subQ0=sQuery(id+"F0.wireOp",EDGE,"E8");var subQ1=sQuery(id+"F0.wireOp",EDGE,"E4");var subQ2=makeQuery(id+"F0.imprint","INTERSECT",VERTEX,{"derivedFrom":[subQ1,subQ0]});Q0=makeQuery(id+"F0.imprint","IMPRINT",FACE,{"disambiguationData":[TD([[makeQuery(id+"F0.imprint","IMPRINT",EDGE,{"disambiguationData":[TD([[subQ2,-1.0]])],"derivedFrom":subQ1}),-1.0]])]});}
            var Q1;
            {var subQ0=sQuery(id+"F0.wireOp",EDGE,"E7");var subQ1=sQuery(id+"F0.wireOp",EDGE,"E2");var subQ2=makeQuery(id+"F0.imprint","INTERSECT",VERTEX,{"derivedFrom":[subQ1,subQ0]});Q1=makeQuery(id+"F0.imprint","IMPRINT",FACE,{"disambiguationData":[TD([[makeQuery(id+"F0.imprint","IMPRINT",EDGE,{"disambiguationData":[TD([[subQ2,-1.0]])],"derivedFrom":subQ1}),-1.0]])]});}
            var Q2;
            {var subQ0=sQuery(id+"F0.wireOp",EDGE,"E7");var subQ1=sQuery(id+"F0.wireOp",EDGE,"E2");var subQ2=makeQuery(id+"F0.imprint","INTERSECT",VERTEX,{"derivedFrom":[subQ1,subQ0]});Q2=makeQuery(id+"F0.imprint","IMPRINT",FACE,{"disambiguationData":[TD([[makeQuery(id+"F0.imprint","IMPRINT",EDGE,{"disambiguationData":[TD([[subQ2,-1.0]])],"derivedFrom":subQ1}),1.0]])]});}
            var Q3;
            {var subQ0=sQuery(id+"F0.wireOp",EDGE,"E8");var subQ1=sQuery(id+"F0.wireOp",EDGE,"E6.2.0");var subQ2=makeQuery(id+"F0.imprint","INTERSECT",VERTEX,{"derivedFrom":[subQ1,subQ0]});Q3=makeQuery(id+"F0.imprint","IMPRINT",FACE,{"disambiguationData":[TD([[makeQuery(id+"F0.imprint","IMPRINT",EDGE,{"disambiguationData":[TD([[subQ2,-1.0]])],"derivedFrom":subQ1}),1.0]])]});}
            var Q4;
            {var subQ0=sQuery(id+"F0.wireOp",EDGE,"E8");var subQ1=sQuery(id+"F0.wireOp",EDGE,"E6.3.0");var subQ2=makeQuery(id+"F0.imprint","INTERSECT",VERTEX,{"derivedFrom":[subQ1,subQ0]});Q4=makeQuery(id+"F0.imprint","IMPRINT",FACE,{"disambiguationData":[TD([[makeQuery(id+"F0.imprint","IMPRINT",EDGE,{"disambiguationData":[TD([[subQ2,-1.0]])],"derivedFrom":subQ1}),1.0]])]});}
            var Q5;
            {var subQ0=sQuery(id+"F0.wireOp",EDGE,"E8");var subQ1=sQuery(id+"F0.wireOp",EDGE,"E6.4.0");var subQ2=makeQuery(id+"F0.imprint","INTERSECT",VERTEX,{"derivedFrom":[subQ1,subQ0]});Q5=makeQuery(id+"F0.imprint","IMPRINT",FACE,{"disambiguationData":[TD([[makeQuery(id+"F0.imprint","IMPRINT",EDGE,{"disambiguationData":[TD([[subQ2,-1.0]])],"derivedFrom":subQ1}),1.0]])]});}
            var Q6;
            {var subQ0=sQuery(id+"F0.wireOp",EDGE,"E8");var subQ1=sQuery(id+"F0.wireOp",EDGE,"E6.5.0");var subQ2=makeQuery(id+"F0.imprint","INTERSECT",VERTEX,{"derivedFrom":[subQ1,subQ0]});Q6=makeQuery(id+"F0.imprint","IMPRINT",FACE,{"disambiguationData":[TD([[makeQuery(id+"F0.imprint","IMPRINT",EDGE,{"disambiguationData":[TD([[subQ2,-1.0]])],"derivedFrom":subQ1}),1.0]])]});}
            var Q7;
            {var subQ0=sQuery(id+"F0.wireOp",EDGE,"E8");var subQ1=sQuery(id+"F0.wireOp",EDGE,"E6.6.0");var subQ2=makeQuery(id+"F0.imprint","INTERSECT",VERTEX,{"derivedFrom":[subQ1,subQ0]});Q7=makeQuery(id+"F0.imprint","IMPRINT",FACE,{"disambiguationData":[TD([[makeQuery(id+"F0.imprint","IMPRINT",EDGE,{"disambiguationData":[TD([[subQ2,-1.0]])],"derivedFrom":subQ1}),1.0]])]});}
            var Q8;
            {var subQ0=sQuery(id+"F0.wireOp",EDGE,"E8");var subQ1=sQuery(id+"F0.wireOp",EDGE,"E6.7.0");var subQ2=makeQuery(id+"F0.imprint","INTERSECT",VERTEX,{"derivedFrom":[subQ1,subQ0]});Q8=makeQuery(id+"F0.imprint","IMPRINT",FACE,{"disambiguationData":[TD([[makeQuery(id+"F0.imprint","IMPRINT",EDGE,{"disambiguationData":[TD([[subQ2,-1.0]])],"derivedFrom":subQ1}),1.0]])]});}
            var Q9;
            {var subQ0=sQuery(id+"F0.wireOp",EDGE,"E8");var subQ1=sQuery(id+"F0.wireOp",EDGE,"E6.8.0");var subQ2=makeQuery(id+"F0.imprint","INTERSECT",VERTEX,{"derivedFrom":[subQ1,subQ0]});Q9=makeQuery(id+"F0.imprint","IMPRINT",FACE,{"disambiguationData":[TD([[makeQuery(id+"F0.imprint","IMPRINT",EDGE,{"disambiguationData":[TD([[subQ2,-1.0]])],"derivedFrom":subQ1}),1.0]])]});}
            var Q10;
            {var subQ0=sQuery(id+"F0.wireOp",EDGE,"E8");var subQ1=sQuery(id+"F0.wireOp",EDGE,"E6.9.0");var subQ2=makeQuery(id+"F0.imprint","INTERSECT",VERTEX,{"derivedFrom":[subQ1,subQ0]});Q10=makeQuery(id+"F0.imprint","IMPRINT",FACE,{"disambiguationData":[TD([[makeQuery(id+"F0.imprint","IMPRINT",EDGE,{"disambiguationData":[TD([[subQ2,-1.0]])],"derivedFrom":subQ1}),1.0]])]});}
            var Q11;
            {var subQ0=sQuery(id+"F0.wireOp",EDGE,"E8");var subQ1=sQuery(id+"F0.wireOp",EDGE,"E6.10.0");var subQ2=makeQuery(id+"F0.imprint","INTERSECT",VERTEX,{"derivedFrom":[subQ1,subQ0]});Q11=makeQuery(id+"F0.imprint","IMPRINT",FACE,{"disambiguationData":[TD([[makeQuery(id+"F0.imprint","IMPRINT",EDGE,{"disambiguationData":[TD([[subQ2,-1.0]])],"derivedFrom":subQ1}),1.0]])]});}
            var Q12;
            {var subQ0=sQuery(id+"F0.wireOp",EDGE,"E8");var subQ1=sQuery(id+"F0.wireOp",EDGE,"E6.11.0");var subQ2=makeQuery(id+"F0.imprint","INTERSECT",VERTEX,{"derivedFrom":[subQ1,subQ0]});Q12=makeQuery(id+"F0.imprint","IMPRINT",FACE,{"disambiguationData":[TD([[makeQuery(id+"F0.imprint","IMPRINT",EDGE,{"disambiguationData":[TD([[subQ2,-1.0]])],"derivedFrom":subQ1}),1.0]])]});}
            var Q13;
            {var subQ0=sQuery(id+"F0.wireOp",EDGE,"E8");var subQ1=sQuery(id+"F0.wireOp",EDGE,"E6.12.0");var subQ2=makeQuery(id+"F0.imprint","INTERSECT",VERTEX,{"derivedFrom":[subQ1,subQ0]});Q13=makeQuery(id+"F0.imprint","IMPRINT",FACE,{"disambiguationData":[TD([[makeQuery(id+"F0.imprint","IMPRINT",EDGE,{"disambiguationData":[TD([[subQ2,-1.0]])],"derivedFrom":subQ1}),1.0]])]});}
            var Q14;
            {var subQ0=sQuery(id+"F0.wireOp",EDGE,"E8");var subQ1=sQuery(id+"F0.wireOp",EDGE,"E3");var subQ2=makeQuery(id+"F0.imprint","INTERSECT",VERTEX,{"derivedFrom":[subQ1,subQ0]});Q14=makeQuery(id+"F0.imprint","IMPRINT",FACE,{"disambiguationData":[TD([[makeQuery(id+"F0.imprint","IMPRINT",EDGE,{"disambiguationData":[TD([[subQ2,-1.0]])],"derivedFrom":subQ1}),-1.0]])]});}
            var Q15;
            {var subQ0=sQuery(id+"F0.wireOp",EDGE,"E8");var subQ1=sQuery(id+"F0.wireOp",EDGE,"E3");var subQ2=makeQuery(id+"F0.imprint","INTERSECT",VERTEX,{"derivedFrom":[subQ1,subQ0]});Q15=makeQuery(id+"F0.imprint","IMPRINT",FACE,{"disambiguationData":[TD([[makeQuery(id+"F0.imprint","IMPRINT",EDGE,{"disambiguationData":[TD([[subQ2,-1.0]])],"derivedFrom":subQ1}),1.0]])]});}
            extrude(context, id + "F3", {"entities" : qUnion([Q0, Q1, Q2, Q3, Q4, Q5, Q6, Q7, Q8, Q9, Q10, Q11, Q12, Q13, Q14, Q15]), "operationType" : NewBodyOperationType.ADD, "endBound" : BoundingType.SYMMETRIC, "depth" : 2.5 * mm, "offsetDistance" : 25 * mm});
        }
        {
            var Q0;
            {var subQ0=sQuery(id+"F0.wireOp",EDGE,"E7");Q0=makeQuery(id+"F3.opExtrude","CAP_EDGE",EDGE,{"disambiguationData":[OSD([subQ0]),TDD([makeQuery(id+"F0.imprint","IMPRINT",EDGE,{"disambiguationData":[TD([[makeQuery(id+"F0.imprint","INTERSECT",VERTEX,{"derivedFrom":[sQuery(id+"F0.wireOp",EDGE,"E6.10.0"),subQ0]}),-1.0]])],"derivedFrom":subQ0})])],"isStart":true});}
            var Q1;
            {var subQ0=sQuery(id+"F0.wireOp",EDGE,"E7");Q1=makeQuery(id+"F3.opExtrude","CAP_EDGE",EDGE,{"disambiguationData":[OSD([subQ0]),TDD([makeQuery(id+"F0.imprint","IMPRINT",EDGE,{"disambiguationData":[TD([[makeQuery(id+"F0.imprint","INTERSECT",VERTEX,{"derivedFrom":[sQuery(id+"F0.wireOp",EDGE,"E6.11.0"),subQ0]}),-1.0]])],"derivedFrom":subQ0})])],"isStart":true});}
            var Q2;
            {var subQ0=sQuery(id+"F0.wireOp",EDGE,"E7");Q2=makeQuery(id+"F3.opExtrude","CAP_EDGE",EDGE,{"disambiguationData":[OSD([subQ0]),TDD([makeQuery(id+"F0.imprint","IMPRINT",EDGE,{"disambiguationData":[TD([[makeQuery(id+"F0.imprint","INTERSECT",VERTEX,{"derivedFrom":[sQuery(id+"F0.wireOp",EDGE,"E6.12.0"),subQ0]}),-1.0]])],"derivedFrom":subQ0})])],"isStart":true});}
            var Q3;
            {var subQ0=sQuery(id+"F0.wireOp",EDGE,"E7");var subQ1=makeQuery(id+"F0.imprint","INTERSECT",VERTEX,{"derivedFrom":[sQuery(id+"F0.wireOp",EDGE,"E3"),subQ0]});Q3=makeQuery(id+"F3.opExtrude","CAP_EDGE",EDGE,{"disambiguationData":[OSD([subQ0]),TDD([makeQuery(id+"F0.imprint","IMPRINT",EDGE,{"disambiguationData":[TD([[subQ1,1.0]])],"derivedFrom":subQ0}),makeQuery(id+"F0.imprint","IMPRINT",EDGE,{"disambiguationData":[TD([[subQ1,-1.0]])],"derivedFrom":subQ0})])],"isStart":true});}
            var Q4;
            {var subQ0=sQuery(id+"F0.wireOp",EDGE,"E7");Q4=makeQuery(id+"F3.opExtrude","CAP_EDGE",EDGE,{"disambiguationData":[OSD([subQ0]),TDD([makeQuery(id+"F0.imprint","IMPRINT",EDGE,{"disambiguationData":[TD([[makeQuery(id+"F0.imprint","INTERSECT",VERTEX,{"derivedFrom":[sQuery(id+"F0.wireOp",EDGE,"E4"),subQ0]}),1.0]])],"derivedFrom":subQ0})])],"isStart":true});}
            var Q5;
            {var subQ0=sQuery(id+"F0.wireOp",EDGE,"E7");var subQ1=makeQuery(id+"F0.imprint","INTERSECT",VERTEX,{"derivedFrom":[sQuery(id+"F0.wireOp",EDGE,"E2"),subQ0]});Q5=makeQuery(id+"F3.opExtrude","CAP_EDGE",EDGE,{"disambiguationData":[OSD([subQ0]),TDD([makeQuery(id+"F0.imprint","IMPRINT",EDGE,{"disambiguationData":[TD([[subQ1,1.0]])],"derivedFrom":subQ0}),makeQuery(id+"F0.imprint","IMPRINT",EDGE,{"disambiguationData":[TD([[subQ1,-1.0]])],"derivedFrom":subQ0})])],"isStart":true});}
            var Q6;
            {var subQ0=sQuery(id+"F0.wireOp",EDGE,"E7");Q6=makeQuery(id+"F3.opExtrude","CAP_EDGE",EDGE,{"disambiguationData":[OSD([subQ0]),TDD([makeQuery(id+"F0.imprint","IMPRINT",EDGE,{"disambiguationData":[TD([[makeQuery(id+"F0.imprint","INTERSECT",VERTEX,{"derivedFrom":[sQuery(id+"F0.wireOp",EDGE,"E6.2.0"),subQ0]}),-1.0]])],"derivedFrom":subQ0})])],"isStart":true});}
            var Q7;
            {var subQ0=sQuery(id+"F0.wireOp",EDGE,"E7");Q7=makeQuery(id+"F3.opExtrude","CAP_EDGE",EDGE,{"disambiguationData":[OSD([subQ0]),TDD([makeQuery(id+"F0.imprint","IMPRINT",EDGE,{"disambiguationData":[TD([[makeQuery(id+"F0.imprint","INTERSECT",VERTEX,{"derivedFrom":[sQuery(id+"F0.wireOp",EDGE,"E6.3.0"),subQ0]}),-1.0]])],"derivedFrom":subQ0})])],"isStart":true});}
            var Q8;
            {var subQ0=sQuery(id+"F0.wireOp",EDGE,"E7");Q8=makeQuery(id+"F3.opExtrude","CAP_EDGE",EDGE,{"disambiguationData":[OSD([subQ0]),TDD([makeQuery(id+"F0.imprint","IMPRINT",EDGE,{"disambiguationData":[TD([[makeQuery(id+"F0.imprint","INTERSECT",VERTEX,{"derivedFrom":[sQuery(id+"F0.wireOp",EDGE,"E6.4.0"),subQ0]}),-1.0]])],"derivedFrom":subQ0})])],"isStart":true});}
            var Q9;
            {var subQ0=sQuery(id+"F0.wireOp",EDGE,"E7");Q9=makeQuery(id+"F3.opExtrude","CAP_EDGE",EDGE,{"disambiguationData":[OSD([subQ0]),TDD([makeQuery(id+"F0.imprint","IMPRINT",EDGE,{"disambiguationData":[TD([[makeQuery(id+"F0.imprint","INTERSECT",VERTEX,{"derivedFrom":[sQuery(id+"F0.wireOp",EDGE,"E6.5.0"),subQ0]}),-1.0]])],"derivedFrom":subQ0})])],"isStart":true});}
            var Q10;
            {var subQ0=sQuery(id+"F0.wireOp",EDGE,"E7");Q10=makeQuery(id+"F3.opExtrude","CAP_EDGE",EDGE,{"disambiguationData":[OSD([subQ0]),TDD([makeQuery(id+"F0.imprint","IMPRINT",EDGE,{"disambiguationData":[TD([[makeQuery(id+"F0.imprint","INTERSECT",VERTEX,{"derivedFrom":[sQuery(id+"F0.wireOp",EDGE,"E6.6.0"),subQ0]}),-1.0]])],"derivedFrom":subQ0})])],"isStart":true});}
            var Q11;
            {var subQ0=sQuery(id+"F0.wireOp",EDGE,"E7");Q11=makeQuery(id+"F3.opExtrude","CAP_EDGE",EDGE,{"disambiguationData":[OSD([subQ0]),TDD([makeQuery(id+"F0.imprint","IMPRINT",EDGE,{"disambiguationData":[TD([[makeQuery(id+"F0.imprint","INTERSECT",VERTEX,{"derivedFrom":[sQuery(id+"F0.wireOp",EDGE,"E6.7.0"),subQ0]}),-1.0]])],"derivedFrom":subQ0})])],"isStart":true});}
            var Q12;
            {var subQ0=sQuery(id+"F0.wireOp",EDGE,"E7");Q12=makeQuery(id+"F3.opExtrude","CAP_EDGE",EDGE,{"disambiguationData":[OSD([subQ0]),TDD([makeQuery(id+"F0.imprint","IMPRINT",EDGE,{"disambiguationData":[TD([[makeQuery(id+"F0.imprint","INTERSECT",VERTEX,{"derivedFrom":[sQuery(id+"F0.wireOp",EDGE,"E6.8.0"),subQ0]}),-1.0]])],"derivedFrom":subQ0})])],"isStart":true});}
            var Q13;
            {var subQ0=sQuery(id+"F0.wireOp",EDGE,"E7");Q13=makeQuery(id+"F3.opExtrude","CAP_EDGE",EDGE,{"disambiguationData":[OSD([subQ0]),TDD([makeQuery(id+"F0.imprint","IMPRINT",EDGE,{"disambiguationData":[TD([[makeQuery(id+"F0.imprint","INTERSECT",VERTEX,{"derivedFrom":[sQuery(id+"F0.wireOp",EDGE,"E6.9.0"),subQ0]}),-1.0]])],"derivedFrom":subQ0})])],"isStart":true});}
            chamfer(context, id + "F4", {"entities" : qUnion([Q0, Q1, Q2, Q3, Q4, Q5, Q6, Q7, Q8, Q9, Q10, Q11, Q12, Q13]), "chamferType" : ChamferType.OFFSET_ANGLE, "width" : 1 * mm, "oppositeDirection" : false, "angle" : 60 * degree});
        }
        {
            var Q0;
            {var subQ0=sQuery(id+"F0.wireOp",EDGE,"E7");Q0=makeQuery(id+"F3.opExtrude","CAP_EDGE",EDGE,{"disambiguationData":[OSD([subQ0]),TDD([makeQuery(id+"F0.imprint","IMPRINT",EDGE,{"disambiguationData":[TD([[makeQuery(id+"F0.imprint","INTERSECT",VERTEX,{"derivedFrom":[sQuery(id+"F0.wireOp",EDGE,"E6.10.0"),subQ0]}),-1.0]])],"derivedFrom":subQ0})])],"isStart":false});}
            var Q1;
            {var subQ0=sQuery(id+"F0.wireOp",EDGE,"E7");Q1=makeQuery(id+"F3.opExtrude","CAP_EDGE",EDGE,{"disambiguationData":[OSD([subQ0]),TDD([makeQuery(id+"F0.imprint","IMPRINT",EDGE,{"disambiguationData":[TD([[makeQuery(id+"F0.imprint","INTERSECT",VERTEX,{"derivedFrom":[sQuery(id+"F0.wireOp",EDGE,"E6.9.0"),subQ0]}),-1.0]])],"derivedFrom":subQ0})])],"isStart":false});}
            var Q2;
            {var subQ0=sQuery(id+"F0.wireOp",EDGE,"E7");Q2=makeQuery(id+"F3.opExtrude","CAP_EDGE",EDGE,{"disambiguationData":[OSD([subQ0]),TDD([makeQuery(id+"F0.imprint","IMPRINT",EDGE,{"disambiguationData":[TD([[makeQuery(id+"F0.imprint","INTERSECT",VERTEX,{"derivedFrom":[sQuery(id+"F0.wireOp",EDGE,"E6.8.0"),subQ0]}),-1.0]])],"derivedFrom":subQ0})])],"isStart":false});}
            var Q3;
            {var subQ0=sQuery(id+"F0.wireOp",EDGE,"E7");Q3=makeQuery(id+"F3.opExtrude","CAP_EDGE",EDGE,{"disambiguationData":[OSD([subQ0]),TDD([makeQuery(id+"F0.imprint","IMPRINT",EDGE,{"disambiguationData":[TD([[makeQuery(id+"F0.imprint","INTERSECT",VERTEX,{"derivedFrom":[sQuery(id+"F0.wireOp",EDGE,"E6.7.0"),subQ0]}),-1.0]])],"derivedFrom":subQ0})])],"isStart":false});}
            var Q4;
            {var subQ0=sQuery(id+"F0.wireOp",EDGE,"E7");Q4=makeQuery(id+"F3.opExtrude","CAP_EDGE",EDGE,{"disambiguationData":[OSD([subQ0]),TDD([makeQuery(id+"F0.imprint","IMPRINT",EDGE,{"disambiguationData":[TD([[makeQuery(id+"F0.imprint","INTERSECT",VERTEX,{"derivedFrom":[sQuery(id+"F0.wireOp",EDGE,"E6.6.0"),subQ0]}),-1.0]])],"derivedFrom":subQ0})])],"isStart":false});}
            var Q5;
            {var subQ0=sQuery(id+"F0.wireOp",EDGE,"E7");Q5=makeQuery(id+"F3.opExtrude","CAP_EDGE",EDGE,{"disambiguationData":[OSD([subQ0]),TDD([makeQuery(id+"F0.imprint","IMPRINT",EDGE,{"disambiguationData":[TD([[makeQuery(id+"F0.imprint","INTERSECT",VERTEX,{"derivedFrom":[sQuery(id+"F0.wireOp",EDGE,"E6.5.0"),subQ0]}),-1.0]])],"derivedFrom":subQ0})])],"isStart":false});}
            var Q6;
            {var subQ0=sQuery(id+"F0.wireOp",EDGE,"E7");Q6=makeQuery(id+"F3.opExtrude","CAP_EDGE",EDGE,{"disambiguationData":[OSD([subQ0]),TDD([makeQuery(id+"F0.imprint","IMPRINT",EDGE,{"disambiguationData":[TD([[makeQuery(id+"F0.imprint","INTERSECT",VERTEX,{"derivedFrom":[sQuery(id+"F0.wireOp",EDGE,"E6.4.0"),subQ0]}),-1.0]])],"derivedFrom":subQ0})])],"isStart":false});}
            var Q7;
            {var subQ0=sQuery(id+"F0.wireOp",EDGE,"E7");Q7=makeQuery(id+"F3.opExtrude","CAP_EDGE",EDGE,{"disambiguationData":[OSD([subQ0]),TDD([makeQuery(id+"F0.imprint","IMPRINT",EDGE,{"disambiguationData":[TD([[makeQuery(id+"F0.imprint","INTERSECT",VERTEX,{"derivedFrom":[sQuery(id+"F0.wireOp",EDGE,"E6.3.0"),subQ0]}),-1.0]])],"derivedFrom":subQ0})])],"isStart":false});}
            var Q8;
            {var subQ0=sQuery(id+"F0.wireOp",EDGE,"E7");Q8=makeQuery(id+"F3.opExtrude","CAP_EDGE",EDGE,{"disambiguationData":[OSD([subQ0]),TDD([makeQuery(id+"F0.imprint","IMPRINT",EDGE,{"disambiguationData":[TD([[makeQuery(id+"F0.imprint","INTERSECT",VERTEX,{"derivedFrom":[sQuery(id+"F0.wireOp",EDGE,"E6.2.0"),subQ0]}),-1.0]])],"derivedFrom":subQ0})])],"isStart":false});}
            var Q9;
            {var subQ0=sQuery(id+"F0.wireOp",EDGE,"E7");var subQ1=makeQuery(id+"F0.imprint","INTERSECT",VERTEX,{"derivedFrom":[sQuery(id+"F0.wireOp",EDGE,"E2"),subQ0]});Q9=makeQuery(id+"F3.opExtrude","CAP_EDGE",EDGE,{"disambiguationData":[OSD([subQ0]),TDD([makeQuery(id+"F0.imprint","IMPRINT",EDGE,{"disambiguationData":[TD([[subQ1,1.0]])],"derivedFrom":subQ0}),makeQuery(id+"F0.imprint","IMPRINT",EDGE,{"disambiguationData":[TD([[subQ1,-1.0]])],"derivedFrom":subQ0})])],"isStart":false});}
            var Q10;
            {var subQ0=sQuery(id+"F0.wireOp",EDGE,"E7");Q10=makeQuery(id+"F3.opExtrude","CAP_EDGE",EDGE,{"disambiguationData":[OSD([subQ0]),TDD([makeQuery(id+"F0.imprint","IMPRINT",EDGE,{"disambiguationData":[TD([[makeQuery(id+"F0.imprint","INTERSECT",VERTEX,{"derivedFrom":[sQuery(id+"F0.wireOp",EDGE,"E4"),subQ0]}),1.0]])],"derivedFrom":subQ0})])],"isStart":false});}
            var Q11;
            {var subQ0=sQuery(id+"F0.wireOp",EDGE,"E7");var subQ1=makeQuery(id+"F0.imprint","INTERSECT",VERTEX,{"derivedFrom":[sQuery(id+"F0.wireOp",EDGE,"E3"),subQ0]});Q11=makeQuery(id+"F3.opExtrude","CAP_EDGE",EDGE,{"disambiguationData":[OSD([subQ0]),TDD([makeQuery(id+"F0.imprint","IMPRINT",EDGE,{"disambiguationData":[TD([[subQ1,1.0]])],"derivedFrom":subQ0}),makeQuery(id+"F0.imprint","IMPRINT",EDGE,{"disambiguationData":[TD([[subQ1,-1.0]])],"derivedFrom":subQ0})])],"isStart":false});}
            var Q12;
            {var subQ0=sQuery(id+"F0.wireOp",EDGE,"E7");Q12=makeQuery(id+"F3.opExtrude","CAP_EDGE",EDGE,{"disambiguationData":[OSD([subQ0]),TDD([makeQuery(id+"F0.imprint","IMPRINT",EDGE,{"disambiguationData":[TD([[makeQuery(id+"F0.imprint","INTERSECT",VERTEX,{"derivedFrom":[sQuery(id+"F0.wireOp",EDGE,"E6.12.0"),subQ0]}),-1.0]])],"derivedFrom":subQ0})])],"isStart":false});}
            var Q13;
            {var subQ0=sQuery(id+"F0.wireOp",EDGE,"E7");Q13=makeQuery(id+"F3.opExtrude","CAP_EDGE",EDGE,{"disambiguationData":[OSD([subQ0]),TDD([makeQuery(id+"F0.imprint","IMPRINT",EDGE,{"disambiguationData":[TD([[makeQuery(id+"F0.imprint","INTERSECT",VERTEX,{"derivedFrom":[sQuery(id+"F0.wireOp",EDGE,"E6.11.0"),subQ0]}),-1.0]])],"derivedFrom":subQ0})])],"isStart":false});}
            chamfer(context, id + "F5", {"entities" : qUnion([Q0, Q1, Q2, Q3, Q4, Q5, Q6, Q7, Q8, Q9, Q10, Q11, Q12, Q13]), "chamferType" : ChamferType.OFFSET_ANGLE, "width" : 1.75 * mm, "oppositeDirection" : false, "angle" : 30 * degree, "tangentPropagation" : true});
        }
        {
            var Q0;
            Q0=makeQuery(id+"F1.opExtrude","CAP_FACE",FACE,{"disambiguationData":[OSD([sQuery(id+"F0.wireOp",EDGE,"E9")])],"isStart":false});
            var sketch = newSketch(context, id + "F6", { "sketchPlane" : qUnion([Q0])});
            skPoint(sketch, "E12.0", {"position": v(-18.75, 75.94) * mm});
            skCircle(sketch, "E13.cCircle", {"center": v(-18.75, 75.94) * mm, "radius": 2.75 * mm, "construction": true});
            skLineSegment(sketch, "E13.0", {"start": v(-16, 75.94) * mm, "end": v(-18.75, 73.19) * mm});
            skLineSegment(sketch, "E13.1", {"start": v(-18.75, 73.19) * mm, "end": v(-21.5, 75.94) * mm});
            skLineSegment(sketch, "E13.2", {"start": v(-21.5, 75.94) * mm, "end": v(-18.75, 78.7) * mm});
            skLineSegment(sketch, "E13.3", {"start": v(-18.75, 78.7) * mm, "end": v(-16, 75.94) * mm});
            skCircle(sketch, "E14", {"center": v(-18.75, 75.94) * mm, "radius": 1 * mm});
            skCircle(sketch, "E15", {"center": v(-18.75, 75.94) * mm, "radius": 3.97 * mm});
            skSolve(sketch);
        }
        {
            var Q0;
            Q0=makeQuery(id+"F6.imprint","IMPRINT",FACE,{"disambiguationData":[TD([[makeQuery(id+"F6.imprint","IMPRINT",EDGE,{"derivedFrom":sQuery(id+"F6.wireOp",EDGE,"E14")}),1.0]])]});
            extrude(context, id + "F7", {"entities" : qUnion([Q0]), "operationType" : NewBodyOperationType.REMOVE, "endBound" : BoundingType.THROUGH_ALL, "oppositeDirection" : true, "depth" : 25 * mm, "offsetDistance" : 25 * mm});
        }
        {
            var Q0;
            Q0=makeQuery(id+"F6.imprint","IMPRINT",FACE,{"disambiguationData":[TD([[makeQuery(id+"F6.imprint","IMPRINT",EDGE,{"derivedFrom":sQuery(id+"F6.wireOp",EDGE,"E13.0")}),1.0]])]});
            extrude(context, id + "F8", {"entities" : qUnion([Q0]), "operationType" : NewBodyOperationType.REMOVE, "oppositeDirection" : true, "depth" : 2 * mm, "offsetDistance" : 25 * mm});
        }
        {
            var Q0;
            Q0=makeQuery(id+"F6.imprint","IMPRINT",FACE,{"disambiguationData":[TD([[makeQuery(id+"F6.imprint","IMPRINT",EDGE,{"derivedFrom":sQuery(id+"F6.wireOp",EDGE,"E13.0")}),-1.0]])]});
            extrude(context, id + "F9", {"entities" : qUnion([Q0]), "operationType" : NewBodyOperationType.REMOVE, "oppositeDirection" : true, "depth" : 3 * mm, "offsetDistance" : 25 * mm});
        }
        {
            var Q0;
            Q0=makeQuery(id+"F9.boolean.opBoolean","COPY",FACE,{"derivedFrom":makeQuery(id+"F9.opExtrude","CAP_FACE",FACE,{"disambiguationData":[OSD([sQuery(id+"F6.wireOp",EDGE,"E13.0"),sQuery(id+"F6.wireOp",EDGE,"E13.1"),sQuery(id+"F6.wireOp",EDGE,"E13.2"),sQuery(id+"F6.wireOp",EDGE,"E13.3"),sQuery(id+"F6.wireOp",EDGE,"E14")])],"isStart":false})});
            var sketch = newSketch(context, id + "F10", { "sketchPlane" : qUnion([Q0])});
            skCircle(sketch, "E16.0", {"center": v(-18.75, 75.94) * mm, "radius": 1 * mm});
            skCircle(sketch, "E17", {"center": v(-18.75, 75.94) * mm, "radius": 1.9 * mm});
            skSolve(sketch);
        }
        {
            var Q0;
            Q0 = qSketchRegion(id + "F10", true);
            extrude(context, id + "F11", {"entities" : qUnion([Q0]), "operationType" : NewBodyOperationType.REMOVE, "oppositeDirection" : true, "depth" : 11.54 * mm, "offsetDistance" : 25 * mm, "hasSecondDirection" : true, "secondDirectionOppositeDirection" : true, "secondDirectionDepth" : 1.8 * mm});
        }
    });
